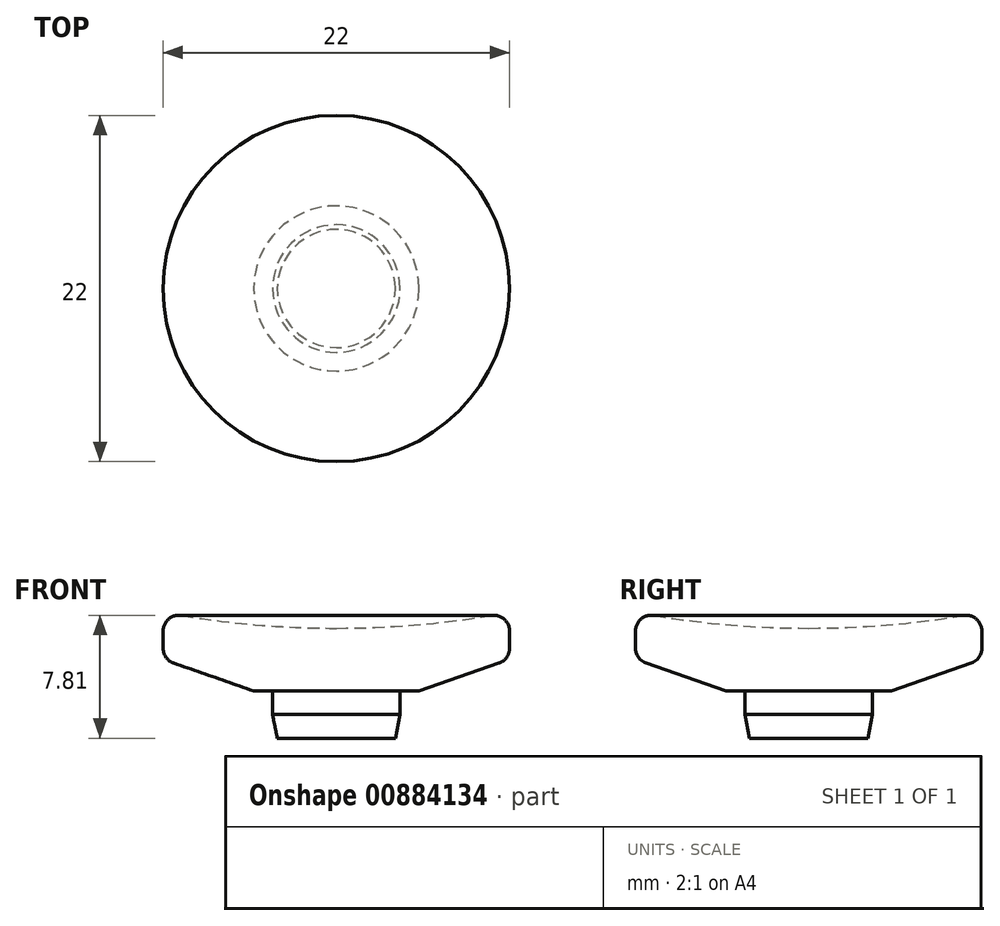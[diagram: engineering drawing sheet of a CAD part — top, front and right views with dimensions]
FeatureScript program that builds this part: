
annotation { "Feature Type Name" : "Feature", "Feature Type Description" : "" }
export const myFeature = defineFeature(function(context is Context, id is Id, definition is map)
    precondition{}
    {
        {
            var Q0;
            Q0=qCreatedBy(makeId("Front.planeOp"),FACE);
            var sketch = newSketch(context, id + "F0", { "sketchPlane" : qUnion([Q0])});
            skLineSegment(sketch, "E0", {"start": v(0, -3.57) * mm, "end": v(0, 7.12) * mm, "construction": true});
            skLineSegment(sketch, "E1", {"start": v(0, 0) * mm, "end": v(4.05, 0) * mm});
            skLineSegment(sketch, "E2", {"start": v(4.05, 0) * mm, "end": v(4.05, 3) * mm});
            skLineSegment(sketch, "E3", {"start": v(4.05, 3) * mm, "end": v(5.25, 3) * mm});
            skLineSegment(sketch, "E4", {"start": v(5.25, 3) * mm, "end": v(11, 5) * mm});
            skLineSegment(sketch, "E5", {"start": v(11, 5) * mm, "end": v(11, 8) * mm});
            skArc(sketch, "E6", {"start": v(11, 8) * mm, "mid": v(5.52, 7.24) * mm, "end": v(0, 6.98) * mm});
            skLineSegment(sketch, "E7.trimOffspring", {"start": v(0, 6.98) * mm, "end": v(0, 0) * mm});
            skPoint(sketch, "E8.start.orphan", {"position": v(0, 8) * mm});
            skSolve(sketch);
        }
        {
            var Q0;
            Q0=qSketchRegion(id+"F0",true);
            var Q1;
            Q1=sQuery(id+"F0.wireOp",EDGE,"E0");
            revolve(context, id + "F1", {"surfaceOperationType" : NewSurfaceOperationType.NEW, "entities" : qUnion([Q0]), "axis" : qUnion([Q1]), "revolveType" : RevolveType.FULL});
        }
        {
            var Q0;
            Q0=makeQuery(id+"F1.opRevolve","SWEPT_EDGE",EDGE,{"disambiguationData":[OSD([sQuery(id+"F0.wireOp",EDGE,"E5"),sQuery(id+"F0.wireOp",EDGE,"33tfvtyz-JtyN-Mw5L-3XGJ-TJyQ87O0g8P3")])]});
            var Q1;
            Q1=makeQuery(id+"F1.opRevolve","SWEPT_EDGE",EDGE,{"disambiguationData":[OSD([sQuery(id+"F0.wireOp",EDGE,"E4"),sQuery(id+"F0.wireOp",EDGE,"E5")])]});
            fillet(context, id + "F2", {"entities" : qUnion([Q0, Q1]), "radius" : 1 * mm, "tangentPropagation" : true, "allowEdgeOverflow" : false});
        }
        {
            var Q0;
            Q0=makeQuery(id+"F1.opRevolve","SWEPT_EDGE",EDGE,{"disambiguationData":[OSD([sQuery(id+"F0.wireOp",EDGE,"E1"),sQuery(id+"F0.wireOp",EDGE,"E2")])]});
            chamfer(context, id + "F3", {"entities" : qUnion([Q0]), "chamferType" : ChamferType.TWO_OFFSETS, "width1" : .3 * mm, "oppositeDirection" : false, "width2" : 1.5 * mm, "tangentPropagation" : true});
        }
    });
